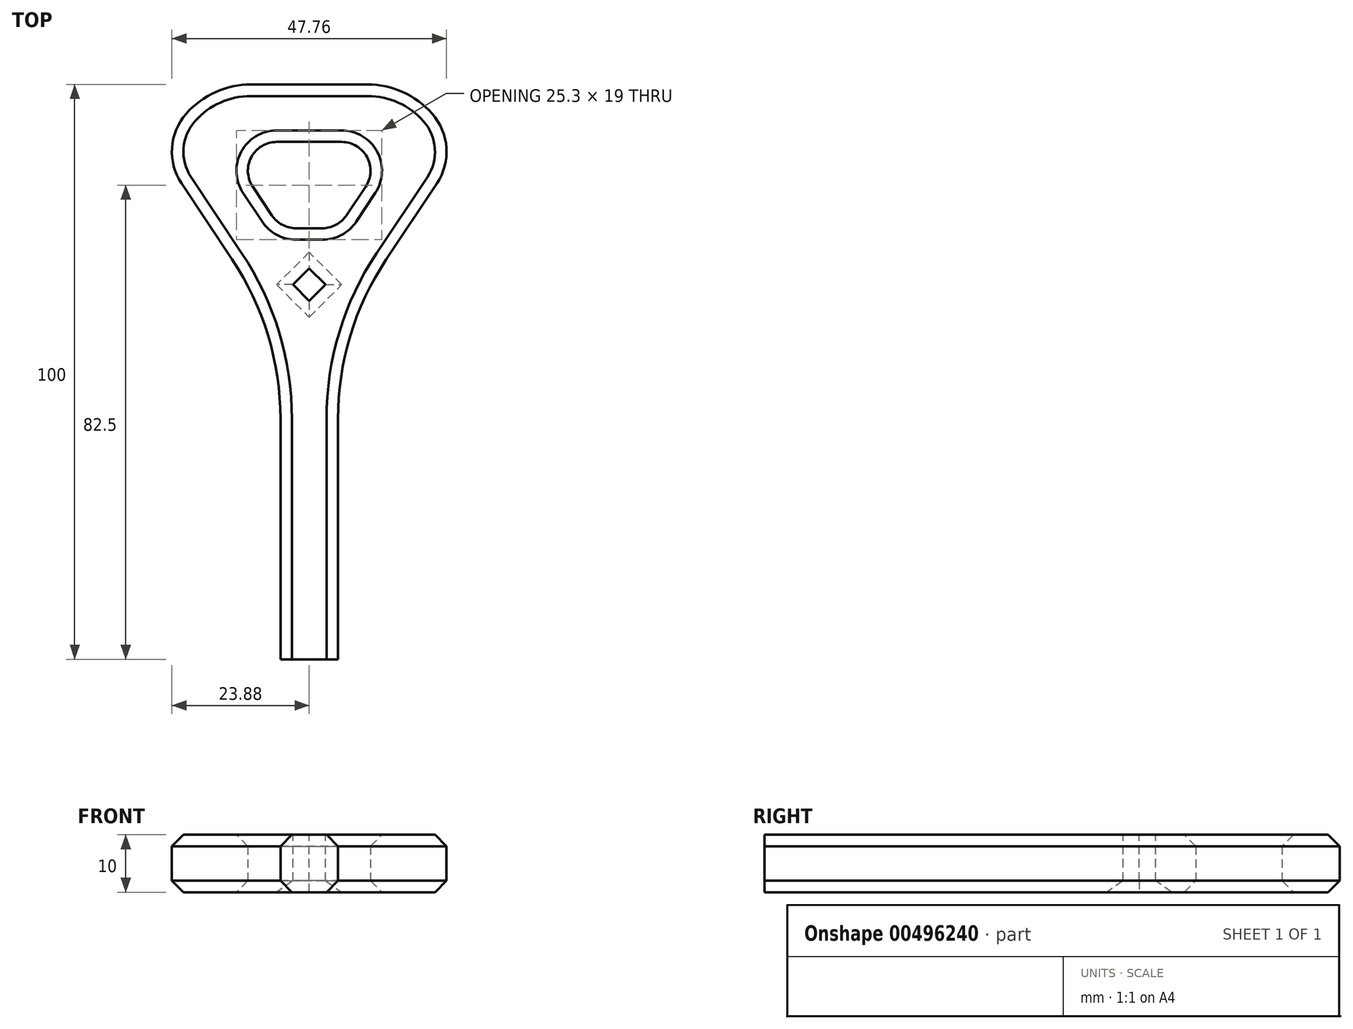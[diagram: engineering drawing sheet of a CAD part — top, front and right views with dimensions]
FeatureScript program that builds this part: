
annotation { "Feature Type Name" : "Feature", "Feature Type Description" : "" }
export const myFeature = defineFeature(function(context is Context, id is Id, definition is map)
    precondition{}
    {
        {
            var Q0;
            Q0=qCreatedBy(makeId("Top.planeOp"),FACE);
            var sketch = newSketch(context, id + "F0", { "sketchPlane" : qUnion([Q0])});
            skLineSegment(sketch, "E0.bottom", {"start": v(-5, 50) * mm, "end": v(5, 50) * mm});
            skLineSegment(sketch, "E0.top", {"start": v(-5, -50) * mm, "end": v(5, -50) * mm});
            skLineSegment(sketch, "E0.left", {"start": v(-5, 31.97) * mm, "end": v(-5, -50) * mm});
            skLineSegment(sketch, "E0.right", {"start": v(5, 31.97) * mm, "end": v(5, -50) * mm});
            skPoint(sketch, "E0.middle", {"position": v(0, 0) * mm});
            skLineSegment(sketch, "E1.bottom", {"start": v(-15, 75) * mm, "end": v(15, 75) * mm});
            skLineSegment(sketch, "E1.top", {"start": v(-15, 65) * mm, "end": v(15, 65) * mm});
            skLineSegment(sketch, "E1.left", {"start": v(-15, 75) * mm, "end": v(-15, 65) * mm});
            skLineSegment(sketch, "E1.right", {"start": v(15, 75) * mm, "end": v(15, 65) * mm});
            skPoint(sketch, "E1.middle", {"position": v(0, 70) * mm});
            skLineSegment(sketch, "E2", {"start": v(-15, 65) * mm, "end": v(-5, 50) * mm});
            skLineSegment(sketch, "E3", {"start": v(5, 50) * mm, "end": v(15, 65) * mm});
            skLineSegment(sketch, "E4", {"start": v(-5, 31.97) * mm, "end": v(-25, 61.97) * mm});
            skLineSegment(sketch, "E5", {"start": v(-25, 61.97) * mm, "end": v(-25, 75) * mm});
            skLineSegment(sketch, "E6", {"start": v(-25, 75) * mm, "end": v(-15, 75) * mm});
            skLineSegment(sketch, "E7.MirrorCS", {"start": v(5, 31.97) * mm, "end": v(25, 61.97) * mm});
            skLineSegment(sketch, "E8.MirrorCS", {"start": v(25, 75) * mm, "end": v(15, 75) * mm});
            skLineSegment(sketch, "E9.MirrorCS", {"start": v(25, 61.97) * mm, "end": v(25, 75) * mm});
            skSolve(sketch);
        }
        {
            var Q0;
            Q0=makeQuery(id+"F0.imprint","IMPRINT",FACE,{"disambiguationData":[TD([[makeQuery(id+"F0.imprint","IMPRINT",EDGE,{"derivedFrom":sQuery(id+"F0.wireOp",EDGE,"E0.bottom")}),-1.0]])]});
            var Q1;
            Q1=makeQuery(id+"F0.imprint","IMPRINT",FACE,{"disambiguationData":[TD([[makeQuery(id+"F0.imprint","IMPRINT",EDGE,{"derivedFrom":sQuery(id+"F0.wireOp",EDGE,"E1.bottom")}),-1.0]])]});
            extrude(context, id + "F1", {"entities" : qUnion([Q0, Q1]), "depth" : 10 * mm});
        }
        {
            var Q0;
            Q0=makeQuery(id+"F1.opExtrude","SWEPT_EDGE",EDGE,{"disambiguationData":[OSD([sQuery(id+"F0.wireOp",EDGE,"E1.top"),sQuery(id+"F0.wireOp",EDGE,"E1.right"),sQuery(id+"F0.wireOp",EDGE,"E3")])]});
            var Q1;
            Q1=makeQuery(id+"F1.opExtrude","SWEPT_EDGE",EDGE,{"disambiguationData":[OSD([sQuery(id+"F0.wireOp",EDGE,"E1.top"),sQuery(id+"F0.wireOp",EDGE,"E1.left"),sQuery(id+"F0.wireOp",EDGE,"E2")])]});
            var Q2;
            Q2=makeQuery(id+"F1.opExtrude","SWEPT_EDGE",EDGE,{"disambiguationData":[OSD([sQuery(id+"F0.wireOp",EDGE,"E0.bottom"),sQuery(id+"F0.wireOp",EDGE,"E2")])]});
            var Q3;
            Q3=makeQuery(id+"F1.opExtrude","SWEPT_EDGE",EDGE,{"disambiguationData":[OSD([sQuery(id+"F0.wireOp",EDGE,"E0.bottom"),sQuery(id+"F0.wireOp",EDGE,"E3")])]});
            fillet(context, id + "F2", {"entities" : qUnion([Q0, Q1, Q2, Q3]), "radius" : 5 * mm, "tangentPropagation" : true, "allowEdgeOverflow" : false});
        }
        {
            var Q0;
            Q0=makeQuery(id+"F1.opExtrude","SWEPT_EDGE",EDGE,{"disambiguationData":[OSD([sQuery(id+"F0.wireOp",EDGE,"E5"),sQuery(id+"F0.wireOp",EDGE,"E6")])]});
            var Q1;
            Q1=makeQuery(id+"F1.opExtrude","SWEPT_EDGE",EDGE,{"disambiguationData":[OSD([sQuery(id+"F0.wireOp",EDGE,"E8.MirrorCS"),sQuery(id+"F0.wireOp",EDGE,"E9.MirrorCS")])]});
            fillet(context, id + "F3", {"entities" : qUnion([Q0, Q1]), "radius" : 15 * mm, "tangentPropagation" : true, "allowEdgeOverflow" : false});
        }
        {
            var Q0;
            Q0=makeQuery(id+"F3.opFillet","BLEND_EDGE",EDGE,{"blendedFrom":[makeQuery(id+"F1.opExtrude","SWEPT_EDGE",EDGE,{"disambiguationData":[OSD([sQuery(id+"F0.wireOp",EDGE,"E5"),sQuery(id+"F0.wireOp",EDGE,"E6")])]}),makeQuery(id+"F1.opExtrude","SWEPT_FACE",FACE,{"disambiguationData":[OSD([sQuery(id+"F0.wireOp",EDGE,"E4")])]})],"blendedInto":[makeQuery(id+"F1.opExtrude","SWEPT_FACE",FACE,{"disambiguationData":[OSD([sQuery(id+"F0.wireOp",EDGE,"E4")])]})]});
            var Q1;
            Q1=makeQuery(id+"F3.opFillet","BLEND_EDGE",EDGE,{"blendedFrom":[makeQuery(id+"F1.opExtrude","SWEPT_EDGE",EDGE,{"disambiguationData":[OSD([sQuery(id+"F0.wireOp",EDGE,"E8.MirrorCS"),sQuery(id+"F0.wireOp",EDGE,"E9.MirrorCS")])]}),makeQuery(id+"F1.opExtrude","SWEPT_FACE",FACE,{"disambiguationData":[OSD([sQuery(id+"F0.wireOp",EDGE,"E7.MirrorCS")])]})],"blendedInto":[makeQuery(id+"F1.opExtrude","SWEPT_FACE",FACE,{"disambiguationData":[OSD([sQuery(id+"F0.wireOp",EDGE,"E7.MirrorCS")])]})]});
            fillet(context, id + "F4", {"entities" : qUnion([Q0, Q1]), "radius" : 10 * mm, "tangentPropagation" : true, "allowEdgeOverflow" : false});
        }
        {
            var Q0;
            Q0=makeQuery(id+"F1.opExtrude","SWEPT_EDGE",EDGE,{"disambiguationData":[OSD([sQuery(id+"F0.wireOp",EDGE,"E0.right"),sQuery(id+"F0.wireOp",EDGE,"E7.MirrorCS")])]});
            var Q1;
            Q1=makeQuery(id+"F1.opExtrude","SWEPT_EDGE",EDGE,{"disambiguationData":[OSD([sQuery(id+"F0.wireOp",EDGE,"E0.left"),sQuery(id+"F0.wireOp",EDGE,"E4")])]});
            fillet(context, id + "F5", {"entities" : qUnion([Q0, Q1]), "radius" : 50 * mm, "tangentPropagation" : true, "allowEdgeOverflow" : false});
        }
        {
            var Q0;
            Q0=makeQuery(id+"F1.opExtrude","CAP_EDGE",EDGE,{"disambiguationData":[OSD([sQuery(id+"F0.wireOp",EDGE,"E1.top")])],"isStart":false});
            var Q1;
            Q1=makeQuery(id+"F1.opExtrude","CAP_EDGE",EDGE,{"disambiguationData":[OSD([sQuery(id+"F0.wireOp",EDGE,"E1.bottom"),sQuery(id+"F0.wireOp",EDGE,"E6"),sQuery(id+"F0.wireOp",EDGE,"E8.MirrorCS")])],"isStart":false});
            var Q2;
            Q2=makeQuery(id+"F1.opExtrude","CAP_EDGE",EDGE,{"disambiguationData":[OSD([sQuery(id+"F0.wireOp",EDGE,"E0.bottom")])],"isStart":true});
            var Q3;
            Q3=makeQuery(id+"F1.opExtrude","CAP_EDGE",EDGE,{"disambiguationData":[OSD([sQuery(id+"F0.wireOp",EDGE,"E1.bottom"),sQuery(id+"F0.wireOp",EDGE,"E6"),sQuery(id+"F0.wireOp",EDGE,"E8.MirrorCS")])],"isStart":true});
            chamfer(context, id + "F6", {"entities" : qUnion([Q0, Q1, Q2, Q3]), "width" : 2 * mm, "tangentPropagation" : true});
        }
        {
            var Q0;
            Q0=makeQuery(id+"F1.opExtrude","CAP_FACE",FACE,{"disambiguationData":[OSD([sQuery(id+"F0.wireOp",EDGE,"E0.bottom"),sQuery(id+"F0.wireOp",EDGE,"E0.top"),sQuery(id+"F0.wireOp",EDGE,"E0.left"),sQuery(id+"F0.wireOp",EDGE,"E0.right"),sQuery(id+"F0.wireOp",EDGE,"E1.bottom"),sQuery(id+"F0.wireOp",EDGE,"E1.top"),sQuery(id+"F0.wireOp",EDGE,"E2"),sQuery(id+"F0.wireOp",EDGE,"E3"),sQuery(id+"F0.wireOp",EDGE,"E4"),sQuery(id+"F0.wireOp",EDGE,"E5"),sQuery(id+"F0.wireOp",EDGE,"E6"),sQuery(id+"F0.wireOp",EDGE,"E7.MirrorCS"),sQuery(id+"F0.wireOp",EDGE,"E8.MirrorCS"),sQuery(id+"F0.wireOp",EDGE,"E9.MirrorCS")])],"isStart":false});
            var sketch = newSketch(context, id + "F7", { "sketchPlane" : qUnion([Q0])});
            skLineSegment(sketch, "E10.bottom", {"start": v(2.83, 40.17) * mm, "end": v(0, 43) * mm});
            skLineSegment(sketch, "E10.top", {"start": v(0, 37.34) * mm, "end": v(-2.83, 40.17) * mm});
            skLineSegment(sketch, "E10.left", {"start": v(2.83, 40.17) * mm, "end": v(0, 37.34) * mm});
            skLineSegment(sketch, "E10.right", {"start": v(0, 43) * mm, "end": v(-2.83, 40.17) * mm});
            skPoint(sketch, "E10.middle", {"position": v(0, 40.17) * mm});
            skSolve(sketch);
        }
        {
            var Q0;
            Q0=makeQuery(id+"F7.imprint","IMPRINT",FACE,{"disambiguationData":[TD([[makeQuery(id+"F7.imprint","IMPRINT",EDGE,{"derivedFrom":sQuery(id+"F7.wireOp",EDGE,"E10.bottom")}),1.0]])]});
            extrude(context, id + "F8", {"entities" : qUnion([Q0]), "operationType" : NewBodyOperationType.REMOVE, "endBound" : BoundingType.THROUGH_ALL, "oppositeDirection" : true, "depth" : 25 * mm});
        }
        {
            var Q0;
            Q0=makeQuery(id+"F8.boolean.opBoolean","COPY",EDGE,{"derivedFrom":makeQuery(id+"F8.opExtrude","CAP_EDGE",EDGE,{"disambiguationData":[OSD([sQuery(id+"F7.wireOp",EDGE,"E10.bottom")])],"isStart":true})});
            var Q1;
            Q1=makeQuery(id+"F8.boolean.opBoolean","COPY",EDGE,{"derivedFrom":makeQuery(id+"F8.opExtrude","CAP_EDGE",EDGE,{"disambiguationData":[OSD([sQuery(id+"F7.wireOp",EDGE,"E10.right")])],"isStart":true})});
            var Q2;
            Q2=makeQuery(id+"F8.boolean.opBoolean","COPY",EDGE,{"derivedFrom":makeQuery(id+"F8.opExtrude","CAP_EDGE",EDGE,{"disambiguationData":[OSD([sQuery(id+"F7.wireOp",EDGE,"E10.left")])],"isStart":true})});
            var Q3;
            Q3=makeQuery(id+"F8.boolean.opBoolean","COPY",EDGE,{"derivedFrom":makeQuery(id+"F8.opExtrude","CAP_EDGE",EDGE,{"disambiguationData":[OSD([sQuery(id+"F7.wireOp",EDGE,"E10.top")])],"isStart":true})});
            var Q4;
            Q4=makeQuery(id+"F8.boolean.opBoolean","INTERSECT",EDGE,{"derivedFrom":[makeQuery(id+"F1.opExtrude","CAP_FACE",FACE,{"disambiguationData":[OSD([sQuery(id+"F0.wireOp",EDGE,"E0.bottom"),sQuery(id+"F0.wireOp",EDGE,"E0.top"),sQuery(id+"F0.wireOp",EDGE,"E0.left"),sQuery(id+"F0.wireOp",EDGE,"E0.right"),sQuery(id+"F0.wireOp",EDGE,"E1.bottom"),sQuery(id+"F0.wireOp",EDGE,"E1.top"),sQuery(id+"F0.wireOp",EDGE,"E2"),sQuery(id+"F0.wireOp",EDGE,"E3"),sQuery(id+"F0.wireOp",EDGE,"E4"),sQuery(id+"F0.wireOp",EDGE,"E5"),sQuery(id+"F0.wireOp",EDGE,"E6"),sQuery(id+"F0.wireOp",EDGE,"E7.MirrorCS"),sQuery(id+"F0.wireOp",EDGE,"E8.MirrorCS"),sQuery(id+"F0.wireOp",EDGE,"E9.MirrorCS")])],"isStart":true}),makeQuery(id+"F8.opExtrude","SWEPT_FACE",FACE,{"disambiguationData":[OSD([sQuery(id+"F7.wireOp",EDGE,"E10.left")])]})]});
            var Q5;
            Q5=makeQuery(id+"F8.boolean.opBoolean","INTERSECT",EDGE,{"derivedFrom":[makeQuery(id+"F1.opExtrude","CAP_FACE",FACE,{"disambiguationData":[OSD([sQuery(id+"F0.wireOp",EDGE,"E0.bottom"),sQuery(id+"F0.wireOp",EDGE,"E0.top"),sQuery(id+"F0.wireOp",EDGE,"E0.left"),sQuery(id+"F0.wireOp",EDGE,"E0.right"),sQuery(id+"F0.wireOp",EDGE,"E1.bottom"),sQuery(id+"F0.wireOp",EDGE,"E1.top"),sQuery(id+"F0.wireOp",EDGE,"E2"),sQuery(id+"F0.wireOp",EDGE,"E3"),sQuery(id+"F0.wireOp",EDGE,"E4"),sQuery(id+"F0.wireOp",EDGE,"E5"),sQuery(id+"F0.wireOp",EDGE,"E6"),sQuery(id+"F0.wireOp",EDGE,"E7.MirrorCS"),sQuery(id+"F0.wireOp",EDGE,"E8.MirrorCS"),sQuery(id+"F0.wireOp",EDGE,"E9.MirrorCS")])],"isStart":true}),makeQuery(id+"F8.opExtrude","SWEPT_FACE",FACE,{"disambiguationData":[OSD([sQuery(id+"F7.wireOp",EDGE,"E10.bottom")])]})]});
            var Q6;
            Q6=makeQuery(id+"F8.boolean.opBoolean","INTERSECT",EDGE,{"derivedFrom":[makeQuery(id+"F1.opExtrude","CAP_FACE",FACE,{"disambiguationData":[OSD([sQuery(id+"F0.wireOp",EDGE,"E0.bottom"),sQuery(id+"F0.wireOp",EDGE,"E0.top"),sQuery(id+"F0.wireOp",EDGE,"E0.left"),sQuery(id+"F0.wireOp",EDGE,"E0.right"),sQuery(id+"F0.wireOp",EDGE,"E1.bottom"),sQuery(id+"F0.wireOp",EDGE,"E1.top"),sQuery(id+"F0.wireOp",EDGE,"E2"),sQuery(id+"F0.wireOp",EDGE,"E3"),sQuery(id+"F0.wireOp",EDGE,"E4"),sQuery(id+"F0.wireOp",EDGE,"E5"),sQuery(id+"F0.wireOp",EDGE,"E6"),sQuery(id+"F0.wireOp",EDGE,"E7.MirrorCS"),sQuery(id+"F0.wireOp",EDGE,"E8.MirrorCS"),sQuery(id+"F0.wireOp",EDGE,"E9.MirrorCS")])],"isStart":true}),makeQuery(id+"F8.opExtrude","SWEPT_FACE",FACE,{"disambiguationData":[OSD([sQuery(id+"F7.wireOp",EDGE,"E10.right")])]})]});
            var Q7;
            Q7=makeQuery(id+"F8.boolean.opBoolean","INTERSECT",EDGE,{"derivedFrom":[makeQuery(id+"F1.opExtrude","CAP_FACE",FACE,{"disambiguationData":[OSD([sQuery(id+"F0.wireOp",EDGE,"E0.bottom"),sQuery(id+"F0.wireOp",EDGE,"E0.top"),sQuery(id+"F0.wireOp",EDGE,"E0.left"),sQuery(id+"F0.wireOp",EDGE,"E0.right"),sQuery(id+"F0.wireOp",EDGE,"E1.bottom"),sQuery(id+"F0.wireOp",EDGE,"E1.top"),sQuery(id+"F0.wireOp",EDGE,"E2"),sQuery(id+"F0.wireOp",EDGE,"E3"),sQuery(id+"F0.wireOp",EDGE,"E4"),sQuery(id+"F0.wireOp",EDGE,"E5"),sQuery(id+"F0.wireOp",EDGE,"E6"),sQuery(id+"F0.wireOp",EDGE,"E7.MirrorCS"),sQuery(id+"F0.wireOp",EDGE,"E8.MirrorCS"),sQuery(id+"F0.wireOp",EDGE,"E9.MirrorCS")])],"isStart":true}),makeQuery(id+"F8.opExtrude","SWEPT_FACE",FACE,{"disambiguationData":[OSD([sQuery(id+"F7.wireOp",EDGE,"E10.top")])]})]});
            chamfer(context, id + "F9", {"entities" : qUnion([Q0, Q1, Q2, Q3, Q4, Q5, Q6, Q7]), "width" : 2 * mm, "tangentPropagation" : true});
        }
        {
            var Q0;
            Q0=makeQuery(id+"F1.opExtrude","SWEPT_FACE",FACE,{"disambiguationData":[OSD([sQuery(id+"F0.wireOp",EDGE,"E0.top")])]});
            extrude(context, id + "F10", {"entities" : qUnion([Q0]), "operationType" : NewBodyOperationType.ADD, "oppositeDirection" : true, "depth" : 16 * mm});
        }
        {
            var Q0;
            Q0=makeQuery(id+"F1.opExtrude","SWEPT_FACE",FACE,{"disambiguationData":[OSD([sQuery(id+"F0.wireOp",EDGE,"E0.top")])]});
            extrude(context, id + "F11", {"entities" : qUnion([Q0]), "operationType" : NewBodyOperationType.REMOVE, "oppositeDirection" : true, "depth" : 25 * mm});
        }
    });
